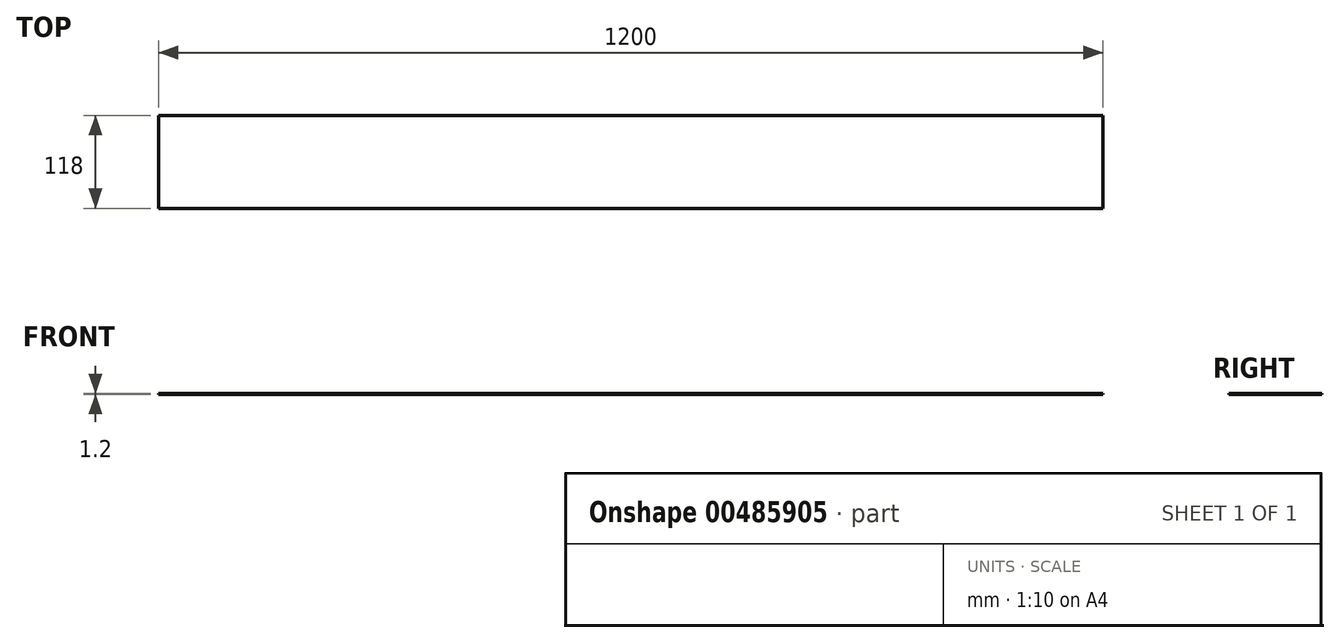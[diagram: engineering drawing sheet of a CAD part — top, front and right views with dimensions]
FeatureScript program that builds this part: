
annotation { "Feature Type Name" : "Feature", "Feature Type Description" : "" }
export const myFeature = defineFeature(function(context is Context, id is Id, definition is map)
    precondition{}
    {
        {
            var Q0;
            Q0=qCreatedBy(makeId("Top.planeOp"),FACE);
            var sketch = newSketch(context, id + "F0", { "sketchPlane" : qUnion([Q0])});
            skLineSegment(sketch, "E0.bottom", {"start": v(600, -59) * mm, "end": v(-600, -59) * mm});
            skLineSegment(sketch, "E0.top", {"start": v(600, 59) * mm, "end": v(-600, 59) * mm});
            skLineSegment(sketch, "E0.left", {"start": v(600, -59) * mm, "end": v(600, 59) * mm});
            skLineSegment(sketch, "E0.right", {"start": v(-600, -59) * mm, "end": v(-600, 59) * mm});
            skPoint(sketch, "E0.middle", {"position": v(0, 0) * mm});
            skSolve(sketch);
        }
        {
            var Q0;
            Q0=qSketchRegion(id+"F0",true);
            extrude(context, id + "F1", {"entities" : qUnion([Q0]), "depth" : 1.2 * mm});
        }
    });
